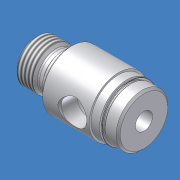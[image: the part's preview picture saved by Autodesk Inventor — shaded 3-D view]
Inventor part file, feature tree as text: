
AUTODESK INVENTOR PART (.ipt)
format: ipt  version: 2012 (Build 160160000, 160)  size: 240,128 bytes
history: native  units: mm (DEFAULTED — no unit token found)
features: other x106, revolve x6, sketch x6, thread x1
ambient origin geometry x8: Origin, YZ Plane, XZ Plane, XY Plane, X Axis, Y Axis, Z Axis, Center Point
bodies: Solid1 (feature_tree)
feature tree (119):
  other  "04R000_rod_guide"
  revolve  "Revolution1"  [1 undecoded]
  thread  "Thread1"  [1 undecoded]
  revolve  "Revolution2"  Angle=360.0deg
  revolve  "Revolution3"  Angle=360.0deg
  revolve  "Revolution4"  [1 undecoded]
  revolve  "Revolution5"  [1 undecoded]
  revolve  "Revolution6"  [1 undecoded]
  other  "s1_XY"
  other  "s1_YZ"
  other  "s1_ZX"
  other  "s1_X"
  other  "s1_Y"
  other  "s1_Z"
  other  "s1_Center"
  other  "s2_XY"
  other  "s2_YZ"
  other  "s2_ZX"
  other  "s2_X"
  other  "s2_Y"
  other  "s2_Z"
  other  "s2_Center"
  other  "dp1_XY"
  other  "dp1_YZ"
  other  "dp1_ZX"
  other  "dp1_X"
  other  "dp1_Y"
  other  "dp1_Z"
  other  "dp1_Center"
  other  "dp2_XY"
  other  "dp2_YZ"
  other  "dp2_ZX"
  other  "dp2_X"
  other  "dp2_Y"
  other  "dp2_Z"
  other  "dp2_Center"
  other  "rod_guide_XY"
  other  "rod_guide_YZ"
  other  "rod_guide_ZX"
  other  "rod_guide_X"
  other  "rod_guide_Y"
  other  "rod_guide_Z"
  other  "rod_guide_Center"
  other  "to_tube_XY"
  other  "to_tube_YZ"
  other  "to_tube_ZX"
  other  "to_tube_X"
  other  "to_tube_Y"
  other  "to_tube_Z"
  other  "to_tube_Center"
  other  "to_foot_bracket_XY"
  other  "to_foot_bracket_YZ"
  other  "to_foot_bracket_ZX"
  other  "to_foot_bracket_X"
  other  "to_foot_bracket_Y"
  other  "to_foot_bracket_Z"
  other  "to_foot_bracket_Center"
  other  "to_nut_XY"
  other  "to_nut_YZ"
  other  "to_nut_ZX"
  other  "to_nut_X"
  other  "to_nut_Y"
  other  "to_nut_Z"
  other  "to_nut_Center"
  other  "to_trunnion_brackets_XY"
  other  "to_trunnion_brackets_YZ"
  other  "to_trunnion_brackets_ZX"
  other  "to_trunnion_brackets_X"
  other  "to_trunnion_brackets_Y"
  other  "to_trunnion_brackets_Z"
  other  "to_trunnion_brackets_Center"
  other  "to_trunnion_brackets1_XY"
  other  "to_trunnion_brackets1_YZ"
  other  "to_trunnion_brackets1_ZX"
  other  "to_trunnion_brackets1_X"
  other  "to_trunnion_brackets1_Y"
  other  "to_trunnion_brackets1_Z"
  other  "to_trunnion_brackets1_Center"
  other  "to_trunnion_brackets2_XY"
  other  "to_trunnion_brackets2_YZ"
  other  "to_trunnion_brackets2_ZX"
  other  "to_trunnion_brackets2_X"
  other  "to_trunnion_brackets2_Y"
  other  "to_trunnion_brackets2_Z"
  other  "to_trunnion_brackets2_Center"
  other  "t111_XY"
  other  "t111_YZ"
  other  "t111_ZX"
  other  "t111_X"
  other  "t111_Y"
  other  "t111_Z"
  other  "t111_Center"
  other  "t1_XY"
  other  "t1_YZ"
  other  "t1_ZX"
  other  "t1_X"
  other  "t1_Y"
  other  "t1_Z"
  other  "t1_Center"
  other  "port_XY"
  other  "port_YZ"
  other  "port_ZX"
  other  "port_X"
  other  "port_Y"
  other  "port_Z"
  other  "port_Center"
  other  "to_screw_XY"
  other  "to_screw_YZ"
  other  "to_screw_ZX"
  other  "to_screw_X"
  other  "to_screw_Y"
  other  "to_screw_Z"
  other  "to_screw_Center"
  sketch  "Sketch_2"  dims[d0=360.0deg d1=5.842127mm d2=0.0mm d3=360.0deg]
  sketch  "Sketch_3"  dims[d4=360.0deg d5=360.0deg]
  sketch  "Sketch_5"  dims[d6=360.0deg d7=360.0deg]
  sketch  "Sketch_10"
  sketch  "Sketch_40"
  sketch  "Sketch_47"
note: 5 required parameter values undecoded (feature->parameter linkage not recoverable at this tier; creation-order binding heuristic only, values carry confidence <= 0.55)